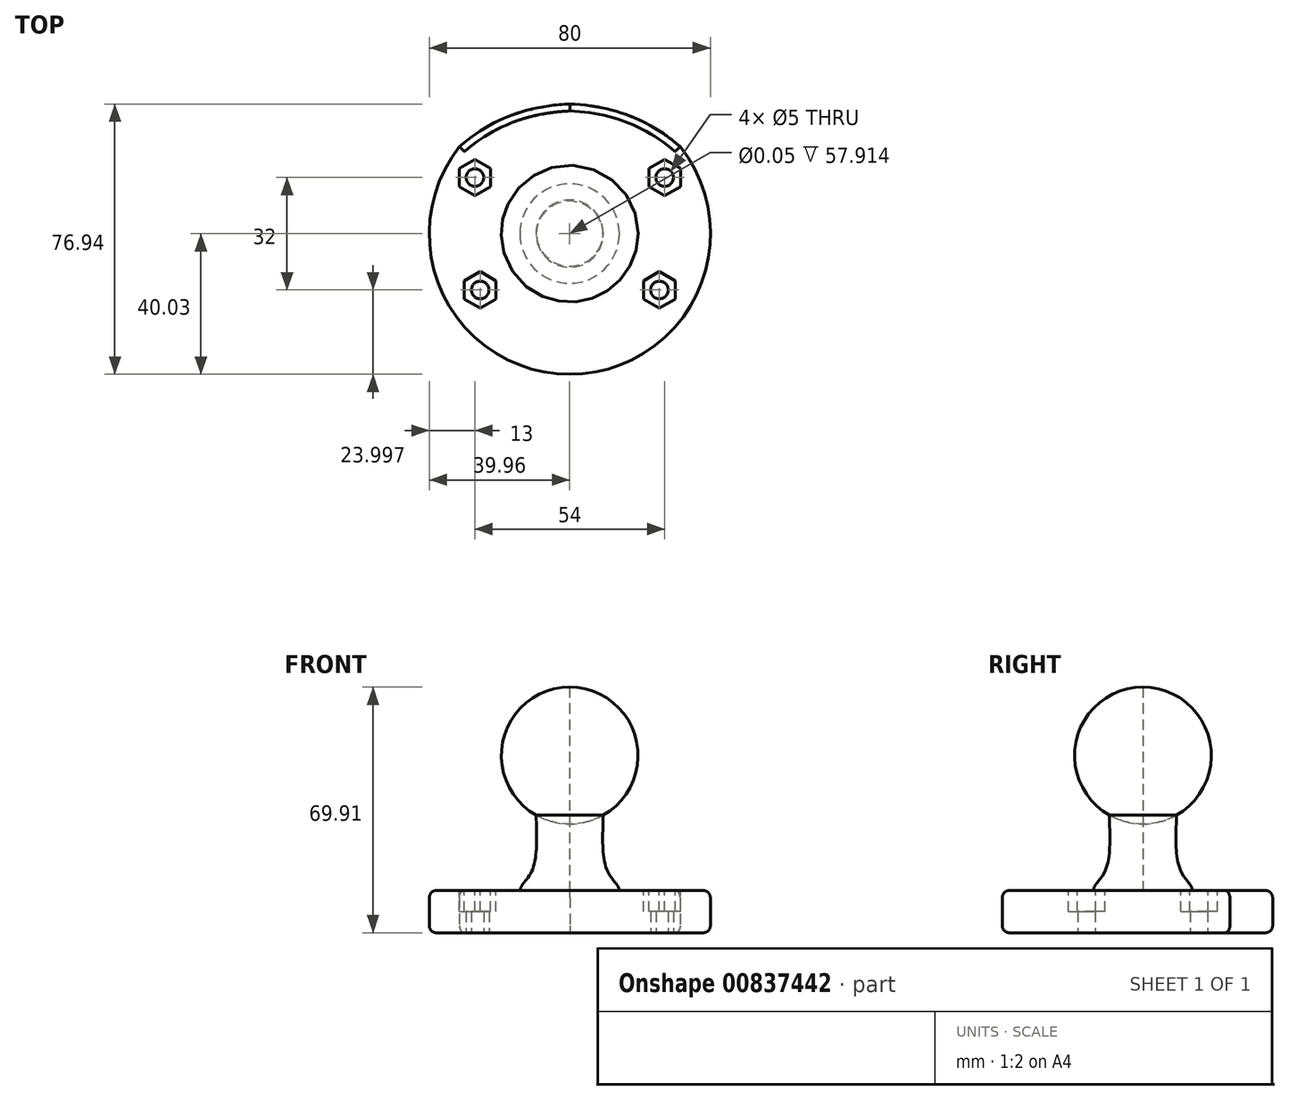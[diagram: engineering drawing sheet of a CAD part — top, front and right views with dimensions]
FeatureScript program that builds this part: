
annotation { "Feature Type Name" : "Feature", "Feature Type Description" : "" }
export const myFeature = defineFeature(function(context is Context, id is Id, definition is map)
    precondition{}
    {
        {
            var Q0;
            Q0=qCreatedBy(makeId("Top.planeOp"),FACE);
            var sketch = newSketch(context, id + "F0", { "sketchPlane" : qUnion([Q0])});
            skPoint(sketch, "E0.middle", {"position": v(0.04, -0.03) * mm});
            skPoint(sketch, "E1.start.orphan", {"position": v(0.04, -40.03) * mm});
            skPoint(sketch, "E2.visualSharp", {"position": v(34.29, 20.63) * mm});
            skPoint(sketch, "E3.visualSharp", {"position": v(-34.53, 20.09) * mm});
            skPoint(sketch, "E4.start.orphan", {"position": v(27.04, -16.03) * mm});
            skPoint(sketch, "E5.start.orphan", {"position": v(-26.96, -16.03) * mm});
            skCircle(sketch, "E6", {"center": v(25.54, -16.03) * mm, "radius": 2.5 * mm});
            skCircle(sketch, "E7", {"center": v(-25.46, -16.03) * mm, "radius": 2.5 * mm});
            skPoint(sketch, "E8.center.orphan", {"position": v(27.04, 15.97) * mm});
            skCircle(sketch, "E9", {"center": v(27.04, 15.97) * mm, "radius": 2.5 * mm});
            skCircle(sketch, "E10", {"center": v(-26.96, 15.97) * mm, "radius": 2.5 * mm});
            skArc(sketch, "E11", {"start": v(-34.53, 20.09) * mm, "mid": v(0.36, -40.03) * mm, "end": v(34.29, 20.63) * mm});
            skPoint(sketch, "E12.endSnap0", {"position": v(0.04, 24.74) * mm});
            skPoint(sketch, "E13.orphan", {"position": v(0.04, 39.97) * mm});
            skPoint(sketch, "E14.visualSharp", {"position": v(31.44, 24.74) * mm});
            skPoint(sketch, "E15.visualSharp", {"position": v(-31.37, 24.74) * mm});
            skLineSegment(sketch, "E16", {"start": v(0.04, -0.03) * mm, "end": v(0.04, 39.97) * mm});
            skArc(sketch, "E17", {"start": v(-31.37, 24.74) * mm, "mid": v(0.04, -40.03) * mm, "end": v(31.44, 24.74) * mm});
            skFitSpline(sketch, "E18", {"points": [v(-31.37, 24.74) * mm, v(0.04, 36.91) * mm, v(31.44, 24.74) * mm], "startDerivative": vector(50.74, 44.21) * mm, "endDerivative": vector(11.96, -59.12) * mm});
            skFitSpline(sketch, "E19.MirrorCS", {"points": [v(31.44, 24.74) * mm, v(0.04, 36.91) * mm, v(-31.37, 24.74) * mm], "startDerivative": vector(-50.74, 44.21) * mm, "endDerivative": vector(-11.96, -59.12) * mm});
            skSolve(sketch);
        }
        {
            var Q0;
            Q0=makeQuery(id+"F0.imprint","IMPRINT",FACE,{"disambiguationData":[TD([[makeQuery(id+"F0.imprint","IMPRINT",EDGE,{"derivedFrom":sQuery(id+"F0.wireOp",EDGE,"E6")}),-1.0]])]});
            extrude(context, id + "F1", {"entities" : qUnion([Q0]), "depth" : 12 * mm, "offsetDistance" : 25 * mm});
        }
        {
            var Q0;
            Q0=qCreatedBy(makeId("Front.planeOp"),FACE);
            var sketch = newSketch(context, id + "F2", { "sketchPlane" : qUnion([Q0])});
            skLineSegment(sketch, "E20", {"start": v(0, 0) * mm, "end": v(0, 101.07) * mm});
            skSolve(sketch);
        }
        {
            var Q0;
            Q0=makeQuery(id+"F1.opExtrude","CAP_FACE",FACE,{"disambiguationData":[OSD([sQuery(id+"F0.wireOp",EDGE,"E6"),sQuery(id+"F0.wireOp",EDGE,"E7"),sQuery(id+"F0.wireOp",EDGE,"E9"),sQuery(id+"F0.wireOp",EDGE,"E10"),sQuery(id+"F0.wireOp",EDGE,"E17"),sQuery(id+"F0.wireOp",EDGE,"E18"),sQuery(id+"F0.wireOp",EDGE,"E19.MirrorCS")])],"isStart":false});
            var sketch = newSketch(context, id + "F3", { "sketchPlane" : qUnion([Q0])});
            skCircle(sketch, "E21.cCircle", {"center": v(-26.96, 15.97) * mm, "radius": 4.5 * mm, "construction": true});
            skLineSegment(sketch, "E21.0", {"start": v(-22.46, 18.56) * mm, "end": v(-22.46, 13.37) * mm});
            skLineSegment(sketch, "E21.1", {"start": v(-22.46, 13.37) * mm, "end": v(-26.96, 10.77) * mm});
            skLineSegment(sketch, "E21.2", {"start": v(-26.96, 10.77) * mm, "end": v(-31.46, 13.37) * mm});
            skLineSegment(sketch, "E21.3", {"start": v(-31.46, 13.37) * mm, "end": v(-31.46, 18.56) * mm});
            skLineSegment(sketch, "E21.4", {"start": v(-31.46, 18.56) * mm, "end": v(-26.96, 21.16) * mm});
            skLineSegment(sketch, "E21.5", {"start": v(-26.96, 21.16) * mm, "end": v(-22.46, 18.56) * mm});
            skPoint(sketch, "E21.0.midPoint", {"position": v(-22.46, 15.97) * mm});
            skCircle(sketch, "E22.cCircle", {"center": v(27.04, 15.97) * mm, "radius": 4.5 * mm, "construction": true});
            skLineSegment(sketch, "E22.0", {"start": v(22.54, 13.37) * mm, "end": v(22.54, 18.56) * mm});
            skLineSegment(sketch, "E22.1", {"start": v(22.54, 18.56) * mm, "end": v(27.04, 21.16) * mm});
            skLineSegment(sketch, "E22.2", {"start": v(27.04, 21.16) * mm, "end": v(31.54, 18.56) * mm});
            skLineSegment(sketch, "E22.3", {"start": v(31.54, 18.56) * mm, "end": v(31.54, 13.37) * mm});
            skLineSegment(sketch, "E22.4", {"start": v(31.54, 13.37) * mm, "end": v(27.04, 10.77) * mm});
            skLineSegment(sketch, "E22.5", {"start": v(27.04, 10.77) * mm, "end": v(22.54, 13.37) * mm});
            skPoint(sketch, "E22.0.midPoint", {"position": v(22.54, 15.97) * mm});
            skCircle(sketch, "E23.cCircle", {"center": v(25.54, -16.03) * mm, "radius": 4.5 * mm, "construction": true});
            skLineSegment(sketch, "E23.0", {"start": v(21.04, -18.63) * mm, "end": v(21.04, -13.44) * mm});
            skLineSegment(sketch, "E23.1", {"start": v(21.04, -13.44) * mm, "end": v(25.54, -10.84) * mm});
            skLineSegment(sketch, "E23.2", {"start": v(25.54, -10.84) * mm, "end": v(30.04, -13.44) * mm});
            skLineSegment(sketch, "E23.3", {"start": v(30.04, -13.44) * mm, "end": v(30.04, -18.63) * mm});
            skLineSegment(sketch, "E23.4", {"start": v(30.04, -18.63) * mm, "end": v(25.54, -21.23) * mm});
            skLineSegment(sketch, "E23.5", {"start": v(25.54, -21.23) * mm, "end": v(21.04, -18.63) * mm});
            skPoint(sketch, "E23.0.midPoint", {"position": v(21.04, -16.03) * mm});
            skCircle(sketch, "E24.cCircle", {"center": v(-25.46, -16.03) * mm, "radius": 4.5 * mm, "construction": true});
            skLineSegment(sketch, "E24.0", {"start": v(-20.96, -13.44) * mm, "end": v(-20.96, -18.63) * mm});
            skLineSegment(sketch, "E24.1", {"start": v(-20.96, -18.63) * mm, "end": v(-25.46, -21.23) * mm});
            skLineSegment(sketch, "E24.2", {"start": v(-25.46, -21.23) * mm, "end": v(-29.96, -18.63) * mm});
            skLineSegment(sketch, "E24.3", {"start": v(-29.96, -18.63) * mm, "end": v(-29.96, -13.44) * mm});
            skLineSegment(sketch, "E24.4", {"start": v(-29.96, -13.44) * mm, "end": v(-25.46, -10.84) * mm});
            skLineSegment(sketch, "E24.5", {"start": v(-25.46, -10.84) * mm, "end": v(-20.96, -13.44) * mm});
            skPoint(sketch, "E24.0.midPoint", {"position": v(-20.96, -16.03) * mm});
            skSolve(sketch);
        }
        {
            var Q0;
            Q0=makeQuery(id+"F3.imprint","IMPRINT",FACE,{"disambiguationData":[TD([[makeQuery(id+"F3.imprint","IMPRINT",EDGE,{"derivedFrom":sQuery(id+"F3.wireOp",EDGE,"E21.0")}),-1.0]])]});
            var Q1;
            Q1=makeQuery(id+"F3.imprint","IMPRINT",FACE,{"disambiguationData":[TD([[makeQuery(id+"F3.imprint","IMPRINT",EDGE,{"derivedFrom":sQuery(id+"F3.wireOp",EDGE,"E22.0")}),-1.0]])]});
            var Q2;
            Q2=makeQuery(id+"F3.imprint","IMPRINT",FACE,{"disambiguationData":[TD([[makeQuery(id+"F3.imprint","IMPRINT",EDGE,{"derivedFrom":sQuery(id+"F3.wireOp",EDGE,"E23.0")}),-1.0]])]});
            var Q3;
            Q3=makeQuery(id+"F3.imprint","IMPRINT",FACE,{"disambiguationData":[TD([[makeQuery(id+"F3.imprint","IMPRINT",EDGE,{"derivedFrom":sQuery(id+"F3.wireOp",EDGE,"E24.0")}),-1.0]])]});
            extrude(context, id + "F4", {"entities" : qUnion([Q0, Q1, Q2, Q3]), "operationType" : NewBodyOperationType.REMOVE, "oppositeDirection" : true, "depth" : 6 * mm, "offsetDistance" : 25 * mm});
        }
        {
            var Q0;
            Q0=makeQuery(id+"F1.opExtrude","CAP_EDGE",EDGE,{"disambiguationData":[OSD([sQuery(id+"F0.wireOp",EDGE,"E17")])],"isStart":false});
            var Q1;
            Q1=makeQuery(id+"F1.opExtrude","CAP_EDGE",EDGE,{"disambiguationData":[OSD([sQuery(id+"F0.wireOp",EDGE,"E17")])],"isStart":true});
            var Q2;
            Q2=makeQuery(id+"F1.opExtrude","CAP_EDGE",EDGE,{"disambiguationData":[OSD([sQuery(id+"F0.wireOp",EDGE,"E19.MirrorCS")])],"isStart":false});
            var Q3;
            Q3=makeQuery(id+"F1.opExtrude","CAP_EDGE",EDGE,{"disambiguationData":[OSD([sQuery(id+"F0.wireOp",EDGE,"E18")])],"isStart":false});
            var Q4;
            Q4=makeQuery(id+"F1.opExtrude","CAP_EDGE",EDGE,{"disambiguationData":[OSD([sQuery(id+"F0.wireOp",EDGE,"E18")])],"isStart":true});
            var Q5;
            Q5=makeQuery(id+"F1.opExtrude","CAP_EDGE",EDGE,{"disambiguationData":[OSD([sQuery(id+"F0.wireOp",EDGE,"E19.MirrorCS")])],"isStart":true});
            fillet(context, id + "F5", {"entities" : qUnion([Q0, Q1, Q2, Q3, Q4, Q5]), "radius" : 2 * mm, "tangentPropagation" : true, "allowEdgeOverflow" : false});
        }
        {
            var Q0;
            Q0=qCreatedBy(makeId("Front.planeOp"),FACE);
            var sketch = newSketch(context, id + "F6", { "sketchPlane" : qUnion([Q0])});
            skLineSegment(sketch, "E25", {"start": v(-0.02, -0.1) * mm, "end": v(-0.02, 58.83) * mm});
            skPoint(sketch, "E26.orphan", {"position": v(-0.02, 54.14) * mm});
            skPoint(sketch, "E27.end.orphan", {"position": v(-0.02, 52.4) * mm});
            skArc(sketch, "E28", {"start": v(-13.74, 64.26) * mm, "mid": v(-19.33, 47.82) * mm, "end": v(-9.58, 33.45) * mm});
            skLineSegment(sketch, "E29", {"start": v(-0.02, 12.5) * mm, "end": v(-0.02, 64.26) * mm});
            skLineSegment(sketch, "E30", {"start": v(-0.02, 11.85) * mm, "end": v(-14.15, 11.85) * mm});
            skPoint(sketch, "E31.1.internal.orphan", {"position": v(-14.15, 14.94) * mm});
            skPoint(sketch, "E32.orphan", {"position": v(-14.15, 12.5) * mm});
            skLineSegment(sketch, "E33", {"start": v(-14.15, 11.85) * mm, "end": v(-14.15, 13.05) * mm});
            skFitSpline(sketch, "E34", {"points": [v(-14.15, 13.05) * mm, v(-10.38, 18.5) * mm, v(-9.58, 33.45) * mm], "startDerivative": vector(11.08, 11.39) * mm, "endDerivative": vector(-1.12, 28.29) * mm});
            skLineSegment(sketch, "E35", {"start": v(-0.02, 25.1) * mm, "end": v(-0.02, 84.4) * mm});
            skArc(sketch, "E36", {"start": v(-0.02, 69.91) * mm, "mid": v(-18.87, 55.37) * mm, "end": v(-9.58, 33.45) * mm});
            skSolve(sketch);
        }
        {
            var Q0;
            {var subQ1=sQuery(id+"F6.wireOp",EDGE,"E29");Q0=makeQuery(id+"F6.imprint","IMPRINT",FACE,{"disambiguationData":[TD([[makeQuery(id+"F6.imprint","IMPRINT",EDGE,{"derivedFrom":subQ1}),1.0]])]});}
            var Q1;
            Q1=sQuery(id+"F2.wireOp",EDGE,"E20");
            revolve(context, id + "F7", {"operationType" : NewBodyOperationType.ADD, "surfaceOperationType" : NewSurfaceOperationType.NEW, "entities" : qUnion([Q0]), "axis" : qUnion([Q1]), "revolveType" : RevolveType.FULL});
        }
        {
            var Q0;
            Q0=makeQuery(id+"F7.opRevolve","SWEPT_EDGE",EDGE,{"disambiguationData":[OSD([sQuery(id+"F6.wireOp",EDGE,"E33"),sQuery(id+"F6.wireOp",EDGE,"E34")])]});
            fillet(context, id + "F8", {"entities" : qUnion([Q0]), "radius" : 5 * mm, "tangentPropagation" : true, "allowEdgeOverflow" : false});
        }
    });
